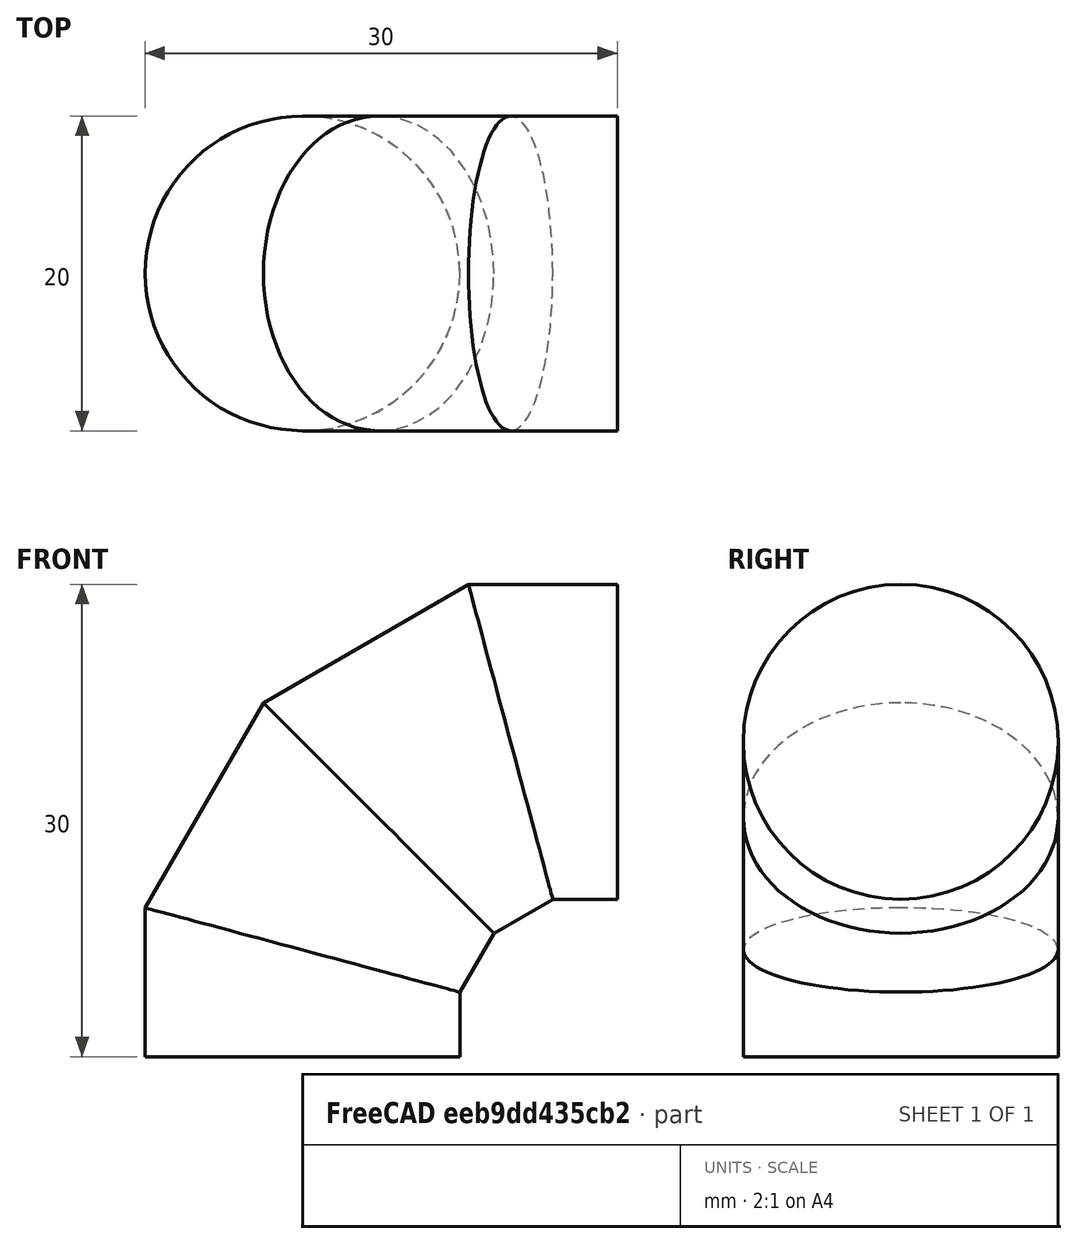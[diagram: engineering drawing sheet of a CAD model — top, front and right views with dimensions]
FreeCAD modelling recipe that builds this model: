
FCSTD DOCUMENT  (FreeCAD 0.17R13247 (Git))
Label: CURVA 90
License: All rights reserved
LicenseURL: http://en.wikipedia.org/wiki/All_rights_reserved
objects: Sketcher::SketchObject×2, PartDesign::Body×1, Part::Sweep×1
note: 4 computed .brp shape members not serialized (recipe doc carries the construction recipe); baked Part::Feature solids carry a one-line shape summary decoded from their .brp

FEATURE [Sketcher::SketchObject] Sketch
  MapMode = 5
  Support = -> [XY_Plane]
  sketch-geometry (1):
    g0: Circle CenterX=0 CenterY=0 CenterZ=0 NormalX=0 NormalY=0 NormalZ=1 AngleXU=0 Radius=10
  constraints (2):
    c: Coincident(g0,g-1)
    c: Radius(g0) = 10
FEATURE [Sketcher::SketchObject] Sketch001
  MapMode = 5
  Placement = pos=(0,0,0) rot=(1,0,0;1.5708rad)
  Support = -> [XZ_Plane]
  sketch-geometry (4):
    g0: LineSegment StartX=0 StartY=0 StartZ=0 EndX=0 EndY=6.77968 EndZ=0
    g1: LineSegment StartX=0 StartY=6.77968 StartZ=0 EndX=4.83897 EndY=15.161 EndZ=0
    g2: LineSegment StartX=4.83897 StartY=15.161 StartZ=0 EndX=13.2203 EndY=20 EndZ=0
    g3: LineSegment StartX=13.2203 StartY=20 StartZ=0 EndX=20 EndY=20 EndZ=0
  constraints (11):
    c: Coincident(g-1,g0)
    c: PointOnObject(g0,g-2)
    c: Coincident(g0,g1)
    c: Coincident(g1,g2)
    c: Coincident(g2,g3)
    c: Horizontal(g3)
    c: Equal(g0,g3)
    c: Equal(g1,g2)
    c: Angle(g2,g3) = 2.61799
    c: Angle(g0,g1) = 2.61799
    c: DistanceY(g-1,g3) = 20
FEATURE [PartDesign::Body] Body
  Group = -> [Sketch,Sketch001]
  Origin = -> Origin
FEATURE [Part::Sweep] Sweep
  Frenet = true
  Sections = -> [Sketch]
  Solid = true
  Spine = -> Sketch001 [Edge1,Edge2,Edge3,Edge4]
  Transition = 1
